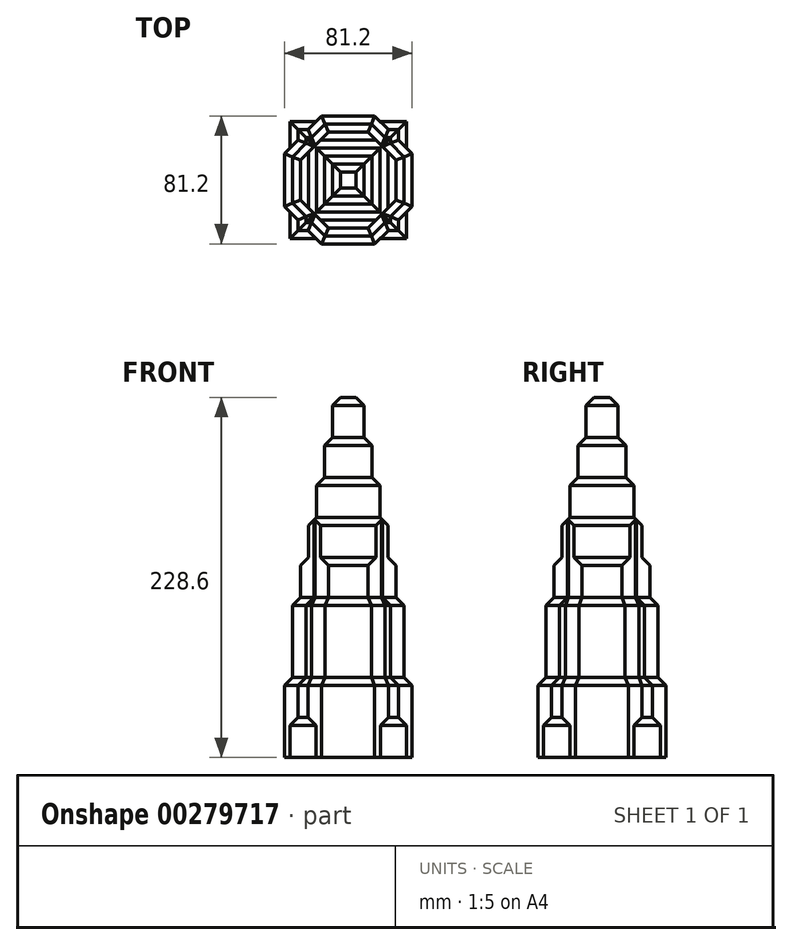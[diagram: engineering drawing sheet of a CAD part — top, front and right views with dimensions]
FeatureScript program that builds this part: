
annotation { "Feature Type Name" : "Feature", "Feature Type Description" : "" }
export const myFeature = defineFeature(function(context is Context, id is Id, definition is map)
    precondition{}
    {
        {
            var Q0;
            Q0=qCreatedBy(makeId("Top.planeOp"),FACE);
            var sketch = newSketch(context, id + "F0", { "sketchPlane" : qUnion([Q0])});
            skCircle(sketch, "E0.cCircle", {"center": v(0, 0) * mm, "radius": 37.05 * mm, "construction": true});
            skLineSegment(sketch, "E0.0", {"start": v(37.05, 37.05) * mm, "end": v(37.05, -37.05) * mm});
            skLineSegment(sketch, "E0.1", {"start": v(37.05, -37.05) * mm, "end": v(-37.05, -37.05) * mm});
            skLineSegment(sketch, "E0.2", {"start": v(-37.05, -37.05) * mm, "end": v(-37.05, 37.05) * mm});
            skLineSegment(sketch, "E0.3", {"start": v(-37.05, 37.05) * mm, "end": v(37.05, 37.05) * mm});
            skPoint(sketch, "E0.0.midPoint", {"position": v(37.05, 0) * mm});
            skCircle(sketch, "E1.cCircle", {"center": v(0, 0) * mm, "radius": 40.6 * mm, "construction": true});
            skLineSegment(sketch, "E1.0", {"start": v(40.6, 16.82) * mm, "end": v(40.6, -16.82) * mm});
            skLineSegment(sketch, "E1.1", {"start": v(40.6, -16.82) * mm, "end": v(16.82, -40.6) * mm});
            skLineSegment(sketch, "E1.2", {"start": v(16.82, -40.6) * mm, "end": v(-16.82, -40.6) * mm});
            skLineSegment(sketch, "E1.3", {"start": v(-16.82, -40.6) * mm, "end": v(-40.6, -16.82) * mm});
            skLineSegment(sketch, "E1.4", {"start": v(-40.6, -16.82) * mm, "end": v(-40.6, 16.82) * mm});
            skLineSegment(sketch, "E1.5", {"start": v(-40.6, 16.82) * mm, "end": v(-16.82, 40.6) * mm});
            skLineSegment(sketch, "E1.6", {"start": v(-16.82, 40.6) * mm, "end": v(16.82, 40.6) * mm});
            skLineSegment(sketch, "E1.7", {"start": v(16.82, 40.6) * mm, "end": v(40.6, 16.82) * mm});
            skPoint(sketch, "E1.0.midPoint", {"position": v(40.6, 0) * mm});
            skSolve(sketch);
        }
        {
            var Q0;
            Q0 = qSketchRegion(id + "F0", true);
            extrude(context, id + "F1", {"entities" : qUnion([Q0]), "depth" : 25.4 * mm});
        }
        {
            var Q0;
            {var subQ0=sQuery(id+"F0.wireOp",EDGE,"E0.3");Q0=makeQuery(id+"F1.opExtrude","CAP_EDGE",EDGE,{"disambiguationData":[OSD([subQ0]),TDD([makeQuery(id+"F0.imprint","IMPRINT",EDGE,{"disambiguationData":[TD([[makeQuery(id+"F0.imprint","INTERSECT",VERTEX,{"derivedFrom":[sQuery(id+"F0.wireOp",EDGE,"E0.2"),subQ0]}),-1.0]])],"derivedFrom":subQ0})])],"isStart":false});}
            var Q1;
            {var subQ0=sQuery(id+"F0.wireOp",EDGE,"E0.2");Q1=makeQuery(id+"F1.opExtrude","CAP_EDGE",EDGE,{"disambiguationData":[OSD([subQ0]),TDD([makeQuery(id+"F0.imprint","IMPRINT",EDGE,{"disambiguationData":[TD([[makeQuery(id+"F0.imprint","INTERSECT",VERTEX,{"derivedFrom":[subQ0,sQuery(id+"F0.wireOp",EDGE,"E0.3")]}),1.0]])],"derivedFrom":subQ0})])],"isStart":false});}
            var Q2;
            {var subQ0=sQuery(id+"F0.wireOp",EDGE,"E0.3");Q2=makeQuery(id+"F1.opExtrude","CAP_EDGE",EDGE,{"disambiguationData":[OSD([subQ0]),TDD([makeQuery(id+"F0.imprint","IMPRINT",EDGE,{"disambiguationData":[TD([[makeQuery(id+"F0.imprint","INTERSECT",VERTEX,{"derivedFrom":[sQuery(id+"F0.wireOp",EDGE,"E0.0"),subQ0]}),1.0]])],"derivedFrom":subQ0})])],"isStart":false});}
            var Q3;
            {var subQ0=sQuery(id+"F0.wireOp",EDGE,"E0.0");Q3=makeQuery(id+"F1.opExtrude","CAP_EDGE",EDGE,{"disambiguationData":[OSD([subQ0]),TDD([makeQuery(id+"F0.imprint","IMPRINT",EDGE,{"disambiguationData":[TD([[makeQuery(id+"F0.imprint","INTERSECT",VERTEX,{"derivedFrom":[subQ0,sQuery(id+"F0.wireOp",EDGE,"E0.3")]}),-1.0]])],"derivedFrom":subQ0})])],"isStart":false});}
            var Q4;
            {var subQ0=sQuery(id+"F0.wireOp",EDGE,"E0.0");Q4=makeQuery(id+"F1.opExtrude","CAP_EDGE",EDGE,{"disambiguationData":[OSD([subQ0]),TDD([makeQuery(id+"F0.imprint","IMPRINT",EDGE,{"disambiguationData":[TD([[makeQuery(id+"F0.imprint","INTERSECT",VERTEX,{"derivedFrom":[subQ0,sQuery(id+"F0.wireOp",EDGE,"E0.1")]}),1.0]])],"derivedFrom":subQ0})])],"isStart":false});}
            var Q5;
            {var subQ0=sQuery(id+"F0.wireOp",EDGE,"E0.1");Q5=makeQuery(id+"F1.opExtrude","CAP_EDGE",EDGE,{"disambiguationData":[OSD([subQ0]),TDD([makeQuery(id+"F0.imprint","IMPRINT",EDGE,{"disambiguationData":[TD([[makeQuery(id+"F0.imprint","INTERSECT",VERTEX,{"derivedFrom":[sQuery(id+"F0.wireOp",EDGE,"E0.0"),subQ0]}),-1.0]])],"derivedFrom":subQ0})])],"isStart":false});}
            var Q6;
            {var subQ0=sQuery(id+"F0.wireOp",EDGE,"E0.1");Q6=makeQuery(id+"F1.opExtrude","CAP_EDGE",EDGE,{"disambiguationData":[OSD([subQ0]),TDD([makeQuery(id+"F0.imprint","IMPRINT",EDGE,{"disambiguationData":[TD([[makeQuery(id+"F0.imprint","INTERSECT",VERTEX,{"derivedFrom":[subQ0,sQuery(id+"F0.wireOp",EDGE,"E0.2")]}),1.0]])],"derivedFrom":subQ0})])],"isStart":false});}
            var Q7;
            {var subQ0=sQuery(id+"F0.wireOp",EDGE,"E0.2");Q7=makeQuery(id+"F1.opExtrude","CAP_EDGE",EDGE,{"disambiguationData":[OSD([subQ0]),TDD([makeQuery(id+"F0.imprint","IMPRINT",EDGE,{"disambiguationData":[TD([[makeQuery(id+"F0.imprint","INTERSECT",VERTEX,{"derivedFrom":[sQuery(id+"F0.wireOp",EDGE,"E0.1"),subQ0]}),-1.0]])],"derivedFrom":subQ0})])],"isStart":false});}
            chamfer(context, id + "F2", {"entities" : qUnion([Q0, Q1, Q2, Q3, Q4, Q5, Q6, Q7]), "width" : 5.08 * mm, "tangentPropagation" : true});
        }
        {
            var Q0;
            Q0=makeQuery(id+"F1.opExtrude","CAP_FACE",FACE,{"disambiguationData":[OSD([sQuery(id+"F0.wireOp",EDGE,"E0.0"),sQuery(id+"F0.wireOp",EDGE,"E0.1"),sQuery(id+"F0.wireOp",EDGE,"E0.2"),sQuery(id+"F0.wireOp",EDGE,"E0.3"),sQuery(id+"F0.wireOp",EDGE,"E1.0"),sQuery(id+"F0.wireOp",EDGE,"E1.1"),sQuery(id+"F0.wireOp",EDGE,"E1.2"),sQuery(id+"F0.wireOp",EDGE,"E1.3"),sQuery(id+"F0.wireOp",EDGE,"E1.4"),sQuery(id+"F0.wireOp",EDGE,"E1.5"),sQuery(id+"F0.wireOp",EDGE,"E1.6"),sQuery(id+"F0.wireOp",EDGE,"E1.7")])],"isStart":false});
            extrude(context, id + "F3", {"entities" : qUnion([Q0]), "operationType" : NewBodyOperationType.ADD, "depth" : 25.4 * mm});
        }
        {
            var Q0;
            Q0=makeQuery(id+"F3.opExtrude","CAP_FACE",FACE,{"disambiguationData":[OSD([sQuery(id+"F0.wireOp",EDGE,"E0.0"),sQuery(id+"F0.wireOp",EDGE,"E0.1"),sQuery(id+"F0.wireOp",EDGE,"E0.2"),sQuery(id+"F0.wireOp",EDGE,"E0.3"),sQuery(id+"F0.wireOp",EDGE,"E1.0"),sQuery(id+"F0.wireOp",EDGE,"E1.1"),sQuery(id+"F0.wireOp",EDGE,"E1.2"),sQuery(id+"F0.wireOp",EDGE,"E1.3"),sQuery(id+"F0.wireOp",EDGE,"E1.4"),sQuery(id+"F0.wireOp",EDGE,"E1.5"),sQuery(id+"F0.wireOp",EDGE,"E1.6"),sQuery(id+"F0.wireOp",EDGE,"E1.7")])],"isStart":false});
            chamfer(context, id + "F4", {"entities" : qUnion([Q0]), "width" : 5.08 * mm, "tangentPropagation" : true});
        }
        {
            var Q0;
            Q0=makeQuery(id+"F3.opExtrude","CAP_FACE",FACE,{"disambiguationData":[OSD([sQuery(id+"F0.wireOp",EDGE,"E0.0"),sQuery(id+"F0.wireOp",EDGE,"E0.1"),sQuery(id+"F0.wireOp",EDGE,"E0.2"),sQuery(id+"F0.wireOp",EDGE,"E0.3"),sQuery(id+"F0.wireOp",EDGE,"E1.0"),sQuery(id+"F0.wireOp",EDGE,"E1.1"),sQuery(id+"F0.wireOp",EDGE,"E1.2"),sQuery(id+"F0.wireOp",EDGE,"E1.3"),sQuery(id+"F0.wireOp",EDGE,"E1.4"),sQuery(id+"F0.wireOp",EDGE,"E1.5"),sQuery(id+"F0.wireOp",EDGE,"E1.6"),sQuery(id+"F0.wireOp",EDGE,"E1.7")])],"isStart":false});
            extrude(context, id + "F5", {"entities" : qUnion([Q0]), "operationType" : NewBodyOperationType.ADD, "depth" : 25.4 * mm});
        }
        {
            var Q0;
            Q0=makeQuery(id+"F5.opExtrude","CAP_FACE",FACE,{"disambiguationData":[OSD([sQuery(id+"F0.wireOp",EDGE,"E0.0"),sQuery(id+"F0.wireOp",EDGE,"E0.1"),sQuery(id+"F0.wireOp",EDGE,"E0.2"),sQuery(id+"F0.wireOp",EDGE,"E0.3"),sQuery(id+"F0.wireOp",EDGE,"E1.0"),sQuery(id+"F0.wireOp",EDGE,"E1.1"),sQuery(id+"F0.wireOp",EDGE,"E1.2"),sQuery(id+"F0.wireOp",EDGE,"E1.3"),sQuery(id+"F0.wireOp",EDGE,"E1.4"),sQuery(id+"F0.wireOp",EDGE,"E1.5"),sQuery(id+"F0.wireOp",EDGE,"E1.6"),sQuery(id+"F0.wireOp",EDGE,"E1.7")])],"isStart":false});
            extrude(context, id + "F6", {"entities" : qUnion([Q0]), "operationType" : NewBodyOperationType.ADD, "depth" : 25.4 * mm});
        }
        {
            var Q0;
            Q0=makeQuery(id+"F6.opExtrude","CAP_FACE",FACE,{"disambiguationData":[OSD([sQuery(id+"F0.wireOp",EDGE,"E0.0"),sQuery(id+"F0.wireOp",EDGE,"E0.1"),sQuery(id+"F0.wireOp",EDGE,"E0.2"),sQuery(id+"F0.wireOp",EDGE,"E0.3"),sQuery(id+"F0.wireOp",EDGE,"E1.0"),sQuery(id+"F0.wireOp",EDGE,"E1.1"),sQuery(id+"F0.wireOp",EDGE,"E1.2"),sQuery(id+"F0.wireOp",EDGE,"E1.3"),sQuery(id+"F0.wireOp",EDGE,"E1.4"),sQuery(id+"F0.wireOp",EDGE,"E1.5"),sQuery(id+"F0.wireOp",EDGE,"E1.6"),sQuery(id+"F0.wireOp",EDGE,"E1.7")])],"isStart":false});
            chamfer(context, id + "F7", {"entities" : qUnion([Q0]), "width" : 5.08 * mm, "tangentPropagation" : true});
        }
        {
            var Q0;
            Q0=makeQuery(id+"F6.opExtrude","CAP_FACE",FACE,{"disambiguationData":[OSD([sQuery(id+"F0.wireOp",EDGE,"E0.0"),sQuery(id+"F0.wireOp",EDGE,"E0.1"),sQuery(id+"F0.wireOp",EDGE,"E0.2"),sQuery(id+"F0.wireOp",EDGE,"E0.3"),sQuery(id+"F0.wireOp",EDGE,"E1.0"),sQuery(id+"F0.wireOp",EDGE,"E1.1"),sQuery(id+"F0.wireOp",EDGE,"E1.2"),sQuery(id+"F0.wireOp",EDGE,"E1.3"),sQuery(id+"F0.wireOp",EDGE,"E1.4"),sQuery(id+"F0.wireOp",EDGE,"E1.5"),sQuery(id+"F0.wireOp",EDGE,"E1.6"),sQuery(id+"F0.wireOp",EDGE,"E1.7")])],"isStart":false});
            extrude(context, id + "F8", {"entities" : qUnion([Q0]), "operationType" : NewBodyOperationType.ADD, "depth" : 25.4 * mm});
        }
        {
            var Q0;
            {var subQ0=sQuery(id+"F0.wireOp",EDGE,"E1.7");var subQ1=sQuery(id+"F0.wireOp",EDGE,"E1.6");var subQ2=sQuery(id+"F0.wireOp",EDGE,"E1.5");var subQ3=sQuery(id+"F0.wireOp",EDGE,"E1.4");var subQ4=sQuery(id+"F0.wireOp",EDGE,"E1.3");var subQ5=sQuery(id+"F0.wireOp",EDGE,"E1.2");var subQ6=sQuery(id+"F0.wireOp",EDGE,"E1.1");var subQ7=sQuery(id+"F0.wireOp",EDGE,"E1.0");var subQ8=sQuery(id+"F0.wireOp",EDGE,"E0.3");var subQ9=sQuery(id+"F0.wireOp",EDGE,"E0.2");var subQ10=sQuery(id+"F0.wireOp",EDGE,"E0.1");var subQ11=sQuery(id+"F0.wireOp",EDGE,"E0.0");Q0=makeQuery(id+"F8.opExtrude","CAP_EDGE",EDGE,{"disambiguationData":[OSD([subQ11,subQ10,subQ9,subQ8,subQ7,subQ6,subQ5,subQ4,subQ3,subQ2,subQ1,subQ0]),TDD([makeQuery(id+"F7.opChamfer","BLEND_EDGE",EDGE,{"blendedFrom":[makeQuery(id+"F6.opExtrude","CAP_EDGE",EDGE,{"disambiguationData":[OSD([subQ11,subQ10,subQ9,subQ8,subQ7,subQ6,subQ5,subQ4,subQ3,subQ2,subQ1,subQ0]),TDD([makeQuery(id+"F5.opExtrude","CAP_EDGE",EDGE,{"disambiguationData":[OSD([subQ11,subQ10,subQ9,subQ8,subQ7,subQ6,subQ5,subQ4,subQ3,subQ2,subQ1,subQ0]),TDD([makeQuery(id+"F4.opChamfer","BLEND_EDGE",EDGE,{"blendedFrom":[makeQuery(id+"F3.opExtrude","CAP_EDGE",EDGE,{"disambiguationData":[OSD([subQ1])],"isStart":false}),makeQuery(id+"F3.opExtrude","CAP_FACE",FACE,{"disambiguationData":[OSD([subQ11,subQ10,subQ9,subQ8,subQ7,subQ6,subQ5,subQ4,subQ3,subQ2,subQ1,subQ0])],"isStart":false})],"blendedInto":[makeQuery(id+"F3.opExtrude","CAP_FACE",FACE,{"disambiguationData":[OSD([subQ11,subQ10,subQ9,subQ8,subQ7,subQ6,subQ5,subQ4,subQ3,subQ2,subQ1,subQ0])],"isStart":false})]})])],"isStart":false})])],"isStart":false}),makeQuery(id+"F6.opExtrude","CAP_FACE",FACE,{"disambiguationData":[OSD([subQ11,subQ10,subQ9,subQ8,subQ7,subQ6,subQ5,subQ4,subQ3,subQ2,subQ1,subQ0])],"isStart":false})],"blendedInto":[makeQuery(id+"F6.opExtrude","CAP_FACE",FACE,{"disambiguationData":[OSD([subQ11,subQ10,subQ9,subQ8,subQ7,subQ6,subQ5,subQ4,subQ3,subQ2,subQ1,subQ0])],"isStart":false})]})])],"isStart":false});}
            var Q1;
            {var subQ0=sQuery(id+"F0.wireOp",EDGE,"E1.7");var subQ1=sQuery(id+"F0.wireOp",EDGE,"E1.6");var subQ2=sQuery(id+"F0.wireOp",EDGE,"E1.5");var subQ3=sQuery(id+"F0.wireOp",EDGE,"E1.4");var subQ4=sQuery(id+"F0.wireOp",EDGE,"E1.3");var subQ5=sQuery(id+"F0.wireOp",EDGE,"E1.2");var subQ6=sQuery(id+"F0.wireOp",EDGE,"E1.1");var subQ7=sQuery(id+"F0.wireOp",EDGE,"E1.0");var subQ8=sQuery(id+"F0.wireOp",EDGE,"E0.3");var subQ9=sQuery(id+"F0.wireOp",EDGE,"E0.2");var subQ10=sQuery(id+"F0.wireOp",EDGE,"E0.1");var subQ11=sQuery(id+"F0.wireOp",EDGE,"E0.0");Q1=makeQuery(id+"F8.opExtrude","CAP_EDGE",EDGE,{"disambiguationData":[OSD([subQ11,subQ10,subQ9,subQ8,subQ7,subQ6,subQ5,subQ4,subQ3,subQ2,subQ1,subQ0]),TDD([makeQuery(id+"F7.opChamfer","BLEND_EDGE",EDGE,{"blendedFrom":[makeQuery(id+"F6.opExtrude","CAP_EDGE",EDGE,{"disambiguationData":[OSD([subQ11,subQ10,subQ9,subQ8,subQ7,subQ6,subQ5,subQ4,subQ3,subQ2,subQ1,subQ0]),TDD([makeQuery(id+"F5.opExtrude","CAP_EDGE",EDGE,{"disambiguationData":[OSD([subQ11,subQ10,subQ9,subQ8,subQ7,subQ6,subQ5,subQ4,subQ3,subQ2,subQ1,subQ0]),TDD([makeQuery(id+"F4.opChamfer","BLEND_EDGE",EDGE,{"blendedFrom":[makeQuery(id+"F3.opExtrude","CAP_EDGE",EDGE,{"disambiguationData":[OSD([subQ3])],"isStart":false}),makeQuery(id+"F3.opExtrude","CAP_FACE",FACE,{"disambiguationData":[OSD([subQ11,subQ10,subQ9,subQ8,subQ7,subQ6,subQ5,subQ4,subQ3,subQ2,subQ1,subQ0])],"isStart":false})],"blendedInto":[makeQuery(id+"F3.opExtrude","CAP_FACE",FACE,{"disambiguationData":[OSD([subQ11,subQ10,subQ9,subQ8,subQ7,subQ6,subQ5,subQ4,subQ3,subQ2,subQ1,subQ0])],"isStart":false})]})])],"isStart":false})])],"isStart":false}),makeQuery(id+"F6.opExtrude","CAP_FACE",FACE,{"disambiguationData":[OSD([subQ11,subQ10,subQ9,subQ8,subQ7,subQ6,subQ5,subQ4,subQ3,subQ2,subQ1,subQ0])],"isStart":false})],"blendedInto":[makeQuery(id+"F6.opExtrude","CAP_FACE",FACE,{"disambiguationData":[OSD([subQ11,subQ10,subQ9,subQ8,subQ7,subQ6,subQ5,subQ4,subQ3,subQ2,subQ1,subQ0])],"isStart":false})]})])],"isStart":false});}
            var Q2;
            {var subQ0=sQuery(id+"F0.wireOp",EDGE,"E1.7");var subQ1=sQuery(id+"F0.wireOp",EDGE,"E1.6");var subQ2=sQuery(id+"F0.wireOp",EDGE,"E1.5");var subQ3=sQuery(id+"F0.wireOp",EDGE,"E1.4");var subQ4=sQuery(id+"F0.wireOp",EDGE,"E1.3");var subQ5=sQuery(id+"F0.wireOp",EDGE,"E1.2");var subQ6=sQuery(id+"F0.wireOp",EDGE,"E1.1");var subQ7=sQuery(id+"F0.wireOp",EDGE,"E1.0");var subQ8=sQuery(id+"F0.wireOp",EDGE,"E0.3");var subQ9=sQuery(id+"F0.wireOp",EDGE,"E0.2");var subQ10=sQuery(id+"F0.wireOp",EDGE,"E0.1");var subQ11=sQuery(id+"F0.wireOp",EDGE,"E0.0");Q2=makeQuery(id+"F8.opExtrude","CAP_EDGE",EDGE,{"disambiguationData":[OSD([subQ11,subQ10,subQ9,subQ8,subQ7,subQ6,subQ5,subQ4,subQ3,subQ2,subQ1,subQ0]),TDD([makeQuery(id+"F7.opChamfer","BLEND_EDGE",EDGE,{"blendedFrom":[makeQuery(id+"F6.opExtrude","CAP_EDGE",EDGE,{"disambiguationData":[OSD([subQ11,subQ10,subQ9,subQ8,subQ7,subQ6,subQ5,subQ4,subQ3,subQ2,subQ1,subQ0]),TDD([makeQuery(id+"F5.opExtrude","CAP_EDGE",EDGE,{"disambiguationData":[OSD([subQ11,subQ10,subQ9,subQ8,subQ7,subQ6,subQ5,subQ4,subQ3,subQ2,subQ1,subQ0]),TDD([makeQuery(id+"F4.opChamfer","BLEND_EDGE",EDGE,{"blendedFrom":[makeQuery(id+"F3.opExtrude","CAP_EDGE",EDGE,{"disambiguationData":[OSD([subQ5])],"isStart":false}),makeQuery(id+"F3.opExtrude","CAP_FACE",FACE,{"disambiguationData":[OSD([subQ11,subQ10,subQ9,subQ8,subQ7,subQ6,subQ5,subQ4,subQ3,subQ2,subQ1,subQ0])],"isStart":false})],"blendedInto":[makeQuery(id+"F3.opExtrude","CAP_FACE",FACE,{"disambiguationData":[OSD([subQ11,subQ10,subQ9,subQ8,subQ7,subQ6,subQ5,subQ4,subQ3,subQ2,subQ1,subQ0])],"isStart":false})]})])],"isStart":false})])],"isStart":false}),makeQuery(id+"F6.opExtrude","CAP_FACE",FACE,{"disambiguationData":[OSD([subQ11,subQ10,subQ9,subQ8,subQ7,subQ6,subQ5,subQ4,subQ3,subQ2,subQ1,subQ0])],"isStart":false})],"blendedInto":[makeQuery(id+"F6.opExtrude","CAP_FACE",FACE,{"disambiguationData":[OSD([subQ11,subQ10,subQ9,subQ8,subQ7,subQ6,subQ5,subQ4,subQ3,subQ2,subQ1,subQ0])],"isStart":false})]})])],"isStart":false});}
            var Q3;
            {var subQ0=sQuery(id+"F0.wireOp",EDGE,"E1.7");var subQ1=sQuery(id+"F0.wireOp",EDGE,"E1.6");var subQ2=sQuery(id+"F0.wireOp",EDGE,"E1.5");var subQ3=sQuery(id+"F0.wireOp",EDGE,"E1.4");var subQ4=sQuery(id+"F0.wireOp",EDGE,"E1.3");var subQ5=sQuery(id+"F0.wireOp",EDGE,"E1.2");var subQ6=sQuery(id+"F0.wireOp",EDGE,"E1.1");var subQ7=sQuery(id+"F0.wireOp",EDGE,"E1.0");var subQ8=sQuery(id+"F0.wireOp",EDGE,"E0.3");var subQ9=sQuery(id+"F0.wireOp",EDGE,"E0.2");var subQ10=sQuery(id+"F0.wireOp",EDGE,"E0.1");var subQ11=sQuery(id+"F0.wireOp",EDGE,"E0.0");Q3=makeQuery(id+"F8.opExtrude","CAP_EDGE",EDGE,{"disambiguationData":[OSD([subQ11,subQ10,subQ9,subQ8,subQ7,subQ6,subQ5,subQ4,subQ3,subQ2,subQ1,subQ0]),TDD([makeQuery(id+"F7.opChamfer","BLEND_EDGE",EDGE,{"blendedFrom":[makeQuery(id+"F6.opExtrude","CAP_EDGE",EDGE,{"disambiguationData":[OSD([subQ11,subQ10,subQ9,subQ8,subQ7,subQ6,subQ5,subQ4,subQ3,subQ2,subQ1,subQ0]),TDD([makeQuery(id+"F5.opExtrude","CAP_EDGE",EDGE,{"disambiguationData":[OSD([subQ11,subQ10,subQ9,subQ8,subQ7,subQ6,subQ5,subQ4,subQ3,subQ2,subQ1,subQ0]),TDD([makeQuery(id+"F4.opChamfer","BLEND_EDGE",EDGE,{"blendedFrom":[makeQuery(id+"F3.opExtrude","CAP_EDGE",EDGE,{"disambiguationData":[OSD([subQ7])],"isStart":false}),makeQuery(id+"F3.opExtrude","CAP_FACE",FACE,{"disambiguationData":[OSD([subQ11,subQ10,subQ9,subQ8,subQ7,subQ6,subQ5,subQ4,subQ3,subQ2,subQ1,subQ0])],"isStart":false})],"blendedInto":[makeQuery(id+"F3.opExtrude","CAP_FACE",FACE,{"disambiguationData":[OSD([subQ11,subQ10,subQ9,subQ8,subQ7,subQ6,subQ5,subQ4,subQ3,subQ2,subQ1,subQ0])],"isStart":false})]})])],"isStart":false})])],"isStart":false}),makeQuery(id+"F6.opExtrude","CAP_FACE",FACE,{"disambiguationData":[OSD([subQ11,subQ10,subQ9,subQ8,subQ7,subQ6,subQ5,subQ4,subQ3,subQ2,subQ1,subQ0])],"isStart":false})],"blendedInto":[makeQuery(id+"F6.opExtrude","CAP_FACE",FACE,{"disambiguationData":[OSD([subQ11,subQ10,subQ9,subQ8,subQ7,subQ6,subQ5,subQ4,subQ3,subQ2,subQ1,subQ0])],"isStart":false})]})])],"isStart":false});}
            chamfer(context, id + "F9", {"entities" : qUnion([Q0, Q1, Q2, Q3]), "width" : 5.08 * mm, "tangentPropagation" : true});
        }
        {
            var Q0;
            Q0=makeQuery(id+"F8.opExtrude","CAP_FACE",FACE,{"disambiguationData":[OSD([sQuery(id+"F0.wireOp",EDGE,"E0.0"),sQuery(id+"F0.wireOp",EDGE,"E0.1"),sQuery(id+"F0.wireOp",EDGE,"E0.2"),sQuery(id+"F0.wireOp",EDGE,"E0.3"),sQuery(id+"F0.wireOp",EDGE,"E1.0"),sQuery(id+"F0.wireOp",EDGE,"E1.1"),sQuery(id+"F0.wireOp",EDGE,"E1.2"),sQuery(id+"F0.wireOp",EDGE,"E1.3"),sQuery(id+"F0.wireOp",EDGE,"E1.4"),sQuery(id+"F0.wireOp",EDGE,"E1.5"),sQuery(id+"F0.wireOp",EDGE,"E1.6"),sQuery(id+"F0.wireOp",EDGE,"E1.7")])],"isStart":false});
            extrude(context, id + "F10", {"entities" : qUnion([Q0]), "operationType" : NewBodyOperationType.ADD, "depth" : 25.4 * mm});
        }
        {
            var Q0;
            {var subQ0=sQuery(id+"F0.wireOp",EDGE,"E1.7");var subQ1=sQuery(id+"F0.wireOp",EDGE,"E1.6");var subQ2=sQuery(id+"F0.wireOp",EDGE,"E1.5");var subQ3=sQuery(id+"F0.wireOp",EDGE,"E1.4");var subQ4=sQuery(id+"F0.wireOp",EDGE,"E1.3");var subQ5=sQuery(id+"F0.wireOp",EDGE,"E1.2");var subQ6=sQuery(id+"F0.wireOp",EDGE,"E1.1");var subQ7=sQuery(id+"F0.wireOp",EDGE,"E1.0");var subQ8=sQuery(id+"F0.wireOp",EDGE,"E0.3");var subQ9=sQuery(id+"F0.wireOp",EDGE,"E0.2");var subQ10=sQuery(id+"F0.wireOp",EDGE,"E0.1");var subQ11=sQuery(id+"F0.wireOp",EDGE,"E0.0");Q0=makeQuery(id+"F10.opExtrude","CAP_EDGE",EDGE,{"disambiguationData":[OSD([subQ11,subQ10,subQ9,subQ8,subQ7,subQ6,subQ5,subQ4,subQ3,subQ2,subQ1,subQ0]),TDD([makeQuery(id+"F9.opChamfer","BLEND_EDGE",EDGE,{"blendedFrom":[makeQuery(id+"F8.opExtrude","CAP_EDGE",EDGE,{"disambiguationData":[OSD([subQ11,subQ10,subQ9,subQ8,subQ7,subQ6,subQ5,subQ4,subQ3,subQ2,subQ1,subQ0]),TDD([makeQuery(id+"F7.opChamfer","BLEND_EDGE",EDGE,{"blendedFrom":[makeQuery(id+"F6.opExtrude","CAP_EDGE",EDGE,{"disambiguationData":[OSD([subQ11,subQ10,subQ9,subQ8,subQ7,subQ6,subQ5,subQ4,subQ3,subQ2,subQ1,subQ0]),TDD([makeQuery(id+"F5.opExtrude","CAP_EDGE",EDGE,{"disambiguationData":[OSD([subQ11,subQ10,subQ9,subQ8,subQ7,subQ6,subQ5,subQ4,subQ3,subQ2,subQ1,subQ0]),TDD([makeQuery(id+"F4.opChamfer","BLEND_EDGE",EDGE,{"blendedFrom":[makeQuery(id+"F3.opExtrude","CAP_EDGE",EDGE,{"disambiguationData":[OSD([subQ1])],"isStart":false}),makeQuery(id+"F3.opExtrude","CAP_FACE",FACE,{"disambiguationData":[OSD([subQ11,subQ10,subQ9,subQ8,subQ7,subQ6,subQ5,subQ4,subQ3,subQ2,subQ1,subQ0])],"isStart":false})],"blendedInto":[makeQuery(id+"F3.opExtrude","CAP_FACE",FACE,{"disambiguationData":[OSD([subQ11,subQ10,subQ9,subQ8,subQ7,subQ6,subQ5,subQ4,subQ3,subQ2,subQ1,subQ0])],"isStart":false})]})])],"isStart":false})])],"isStart":false}),makeQuery(id+"F6.opExtrude","CAP_FACE",FACE,{"disambiguationData":[OSD([subQ11,subQ10,subQ9,subQ8,subQ7,subQ6,subQ5,subQ4,subQ3,subQ2,subQ1,subQ0])],"isStart":false})],"blendedInto":[makeQuery(id+"F6.opExtrude","CAP_FACE",FACE,{"disambiguationData":[OSD([subQ11,subQ10,subQ9,subQ8,subQ7,subQ6,subQ5,subQ4,subQ3,subQ2,subQ1,subQ0])],"isStart":false})]})])],"isStart":false}),makeQuery(id+"F8.opExtrude","CAP_FACE",FACE,{"disambiguationData":[OSD([subQ11,subQ10,subQ9,subQ8,subQ7,subQ6,subQ5,subQ4,subQ3,subQ2,subQ1,subQ0])],"isStart":false})],"blendedInto":[makeQuery(id+"F8.opExtrude","CAP_FACE",FACE,{"disambiguationData":[OSD([subQ11,subQ10,subQ9,subQ8,subQ7,subQ6,subQ5,subQ4,subQ3,subQ2,subQ1,subQ0])],"isStart":false})]})])],"isStart":false});}
            var Q1;
            {var subQ0=sQuery(id+"F0.wireOp",EDGE,"E1.7");var subQ1=sQuery(id+"F0.wireOp",EDGE,"E1.6");var subQ2=sQuery(id+"F0.wireOp",EDGE,"E1.5");var subQ3=sQuery(id+"F0.wireOp",EDGE,"E1.4");var subQ4=sQuery(id+"F0.wireOp",EDGE,"E1.3");var subQ5=sQuery(id+"F0.wireOp",EDGE,"E1.2");var subQ6=sQuery(id+"F0.wireOp",EDGE,"E1.1");var subQ7=sQuery(id+"F0.wireOp",EDGE,"E1.0");var subQ8=sQuery(id+"F0.wireOp",EDGE,"E0.3");var subQ9=sQuery(id+"F0.wireOp",EDGE,"E0.2");var subQ10=sQuery(id+"F0.wireOp",EDGE,"E0.1");var subQ11=sQuery(id+"F0.wireOp",EDGE,"E0.0");Q1=makeQuery(id+"F10.opExtrude","CAP_EDGE",EDGE,{"disambiguationData":[OSD([subQ11,subQ10,subQ9,subQ8,subQ7,subQ6,subQ5,subQ4,subQ3,subQ2,subQ1,subQ0]),TDD([makeQuery(id+"F9.opChamfer","BLEND_EDGE",EDGE,{"blendedFrom":[makeQuery(id+"F8.opExtrude","CAP_EDGE",EDGE,{"disambiguationData":[OSD([subQ11,subQ10,subQ9,subQ8,subQ7,subQ6,subQ5,subQ4,subQ3,subQ2,subQ1,subQ0]),TDD([makeQuery(id+"F7.opChamfer","BLEND_EDGE",EDGE,{"blendedFrom":[makeQuery(id+"F6.opExtrude","CAP_EDGE",EDGE,{"disambiguationData":[OSD([subQ11,subQ10,subQ9,subQ8,subQ7,subQ6,subQ5,subQ4,subQ3,subQ2,subQ1,subQ0]),TDD([makeQuery(id+"F5.opExtrude","CAP_EDGE",EDGE,{"disambiguationData":[OSD([subQ11,subQ10,subQ9,subQ8,subQ7,subQ6,subQ5,subQ4,subQ3,subQ2,subQ1,subQ0]),TDD([makeQuery(id+"F4.opChamfer","BLEND_EDGE",EDGE,{"blendedFrom":[makeQuery(id+"F3.opExtrude","CAP_EDGE",EDGE,{"disambiguationData":[OSD([subQ3])],"isStart":false}),makeQuery(id+"F3.opExtrude","CAP_FACE",FACE,{"disambiguationData":[OSD([subQ11,subQ10,subQ9,subQ8,subQ7,subQ6,subQ5,subQ4,subQ3,subQ2,subQ1,subQ0])],"isStart":false})],"blendedInto":[makeQuery(id+"F3.opExtrude","CAP_FACE",FACE,{"disambiguationData":[OSD([subQ11,subQ10,subQ9,subQ8,subQ7,subQ6,subQ5,subQ4,subQ3,subQ2,subQ1,subQ0])],"isStart":false})]})])],"isStart":false})])],"isStart":false}),makeQuery(id+"F6.opExtrude","CAP_FACE",FACE,{"disambiguationData":[OSD([subQ11,subQ10,subQ9,subQ8,subQ7,subQ6,subQ5,subQ4,subQ3,subQ2,subQ1,subQ0])],"isStart":false})],"blendedInto":[makeQuery(id+"F6.opExtrude","CAP_FACE",FACE,{"disambiguationData":[OSD([subQ11,subQ10,subQ9,subQ8,subQ7,subQ6,subQ5,subQ4,subQ3,subQ2,subQ1,subQ0])],"isStart":false})]})])],"isStart":false}),makeQuery(id+"F8.opExtrude","CAP_FACE",FACE,{"disambiguationData":[OSD([subQ11,subQ10,subQ9,subQ8,subQ7,subQ6,subQ5,subQ4,subQ3,subQ2,subQ1,subQ0])],"isStart":false})],"blendedInto":[makeQuery(id+"F8.opExtrude","CAP_FACE",FACE,{"disambiguationData":[OSD([subQ11,subQ10,subQ9,subQ8,subQ7,subQ6,subQ5,subQ4,subQ3,subQ2,subQ1,subQ0])],"isStart":false})]})])],"isStart":false});}
            var Q2;
            {var subQ0=sQuery(id+"F0.wireOp",EDGE,"E1.7");var subQ1=sQuery(id+"F0.wireOp",EDGE,"E1.6");var subQ2=sQuery(id+"F0.wireOp",EDGE,"E1.5");var subQ3=sQuery(id+"F0.wireOp",EDGE,"E1.4");var subQ4=sQuery(id+"F0.wireOp",EDGE,"E1.3");var subQ5=sQuery(id+"F0.wireOp",EDGE,"E1.2");var subQ6=sQuery(id+"F0.wireOp",EDGE,"E1.1");var subQ7=sQuery(id+"F0.wireOp",EDGE,"E1.0");var subQ8=sQuery(id+"F0.wireOp",EDGE,"E0.3");var subQ9=sQuery(id+"F0.wireOp",EDGE,"E0.2");var subQ10=sQuery(id+"F0.wireOp",EDGE,"E0.1");var subQ11=sQuery(id+"F0.wireOp",EDGE,"E0.0");Q2=makeQuery(id+"F10.opExtrude","CAP_EDGE",EDGE,{"disambiguationData":[OSD([subQ11,subQ10,subQ9,subQ8,subQ7,subQ6,subQ5,subQ4,subQ3,subQ2,subQ1,subQ0]),TDD([makeQuery(id+"F9.opChamfer","BLEND_EDGE",EDGE,{"blendedFrom":[makeQuery(id+"F8.opExtrude","CAP_EDGE",EDGE,{"disambiguationData":[OSD([subQ11,subQ10,subQ9,subQ8,subQ7,subQ6,subQ5,subQ4,subQ3,subQ2,subQ1,subQ0]),TDD([makeQuery(id+"F7.opChamfer","BLEND_EDGE",EDGE,{"blendedFrom":[makeQuery(id+"F6.opExtrude","CAP_EDGE",EDGE,{"disambiguationData":[OSD([subQ11,subQ10,subQ9,subQ8,subQ7,subQ6,subQ5,subQ4,subQ3,subQ2,subQ1,subQ0]),TDD([makeQuery(id+"F5.opExtrude","CAP_EDGE",EDGE,{"disambiguationData":[OSD([subQ11,subQ10,subQ9,subQ8,subQ7,subQ6,subQ5,subQ4,subQ3,subQ2,subQ1,subQ0]),TDD([makeQuery(id+"F4.opChamfer","BLEND_EDGE",EDGE,{"blendedFrom":[makeQuery(id+"F3.opExtrude","CAP_EDGE",EDGE,{"disambiguationData":[OSD([subQ5])],"isStart":false}),makeQuery(id+"F3.opExtrude","CAP_FACE",FACE,{"disambiguationData":[OSD([subQ11,subQ10,subQ9,subQ8,subQ7,subQ6,subQ5,subQ4,subQ3,subQ2,subQ1,subQ0])],"isStart":false})],"blendedInto":[makeQuery(id+"F3.opExtrude","CAP_FACE",FACE,{"disambiguationData":[OSD([subQ11,subQ10,subQ9,subQ8,subQ7,subQ6,subQ5,subQ4,subQ3,subQ2,subQ1,subQ0])],"isStart":false})]})])],"isStart":false})])],"isStart":false}),makeQuery(id+"F6.opExtrude","CAP_FACE",FACE,{"disambiguationData":[OSD([subQ11,subQ10,subQ9,subQ8,subQ7,subQ6,subQ5,subQ4,subQ3,subQ2,subQ1,subQ0])],"isStart":false})],"blendedInto":[makeQuery(id+"F6.opExtrude","CAP_FACE",FACE,{"disambiguationData":[OSD([subQ11,subQ10,subQ9,subQ8,subQ7,subQ6,subQ5,subQ4,subQ3,subQ2,subQ1,subQ0])],"isStart":false})]})])],"isStart":false}),makeQuery(id+"F8.opExtrude","CAP_FACE",FACE,{"disambiguationData":[OSD([subQ11,subQ10,subQ9,subQ8,subQ7,subQ6,subQ5,subQ4,subQ3,subQ2,subQ1,subQ0])],"isStart":false})],"blendedInto":[makeQuery(id+"F8.opExtrude","CAP_FACE",FACE,{"disambiguationData":[OSD([subQ11,subQ10,subQ9,subQ8,subQ7,subQ6,subQ5,subQ4,subQ3,subQ2,subQ1,subQ0])],"isStart":false})]})])],"isStart":false});}
            var Q3;
            {var subQ0=sQuery(id+"F0.wireOp",EDGE,"E1.7");var subQ1=sQuery(id+"F0.wireOp",EDGE,"E1.6");var subQ2=sQuery(id+"F0.wireOp",EDGE,"E1.5");var subQ3=sQuery(id+"F0.wireOp",EDGE,"E1.4");var subQ4=sQuery(id+"F0.wireOp",EDGE,"E1.3");var subQ5=sQuery(id+"F0.wireOp",EDGE,"E1.2");var subQ6=sQuery(id+"F0.wireOp",EDGE,"E1.1");var subQ7=sQuery(id+"F0.wireOp",EDGE,"E1.0");var subQ8=sQuery(id+"F0.wireOp",EDGE,"E0.3");var subQ9=sQuery(id+"F0.wireOp",EDGE,"E0.2");var subQ10=sQuery(id+"F0.wireOp",EDGE,"E0.1");var subQ11=sQuery(id+"F0.wireOp",EDGE,"E0.0");Q3=makeQuery(id+"F10.opExtrude","CAP_EDGE",EDGE,{"disambiguationData":[OSD([subQ11,subQ10,subQ9,subQ8,subQ7,subQ6,subQ5,subQ4,subQ3,subQ2,subQ1,subQ0]),TDD([makeQuery(id+"F9.opChamfer","BLEND_EDGE",EDGE,{"blendedFrom":[makeQuery(id+"F8.opExtrude","CAP_EDGE",EDGE,{"disambiguationData":[OSD([subQ11,subQ10,subQ9,subQ8,subQ7,subQ6,subQ5,subQ4,subQ3,subQ2,subQ1,subQ0]),TDD([makeQuery(id+"F7.opChamfer","BLEND_EDGE",EDGE,{"blendedFrom":[makeQuery(id+"F6.opExtrude","CAP_EDGE",EDGE,{"disambiguationData":[OSD([subQ11,subQ10,subQ9,subQ8,subQ7,subQ6,subQ5,subQ4,subQ3,subQ2,subQ1,subQ0]),TDD([makeQuery(id+"F5.opExtrude","CAP_EDGE",EDGE,{"disambiguationData":[OSD([subQ11,subQ10,subQ9,subQ8,subQ7,subQ6,subQ5,subQ4,subQ3,subQ2,subQ1,subQ0]),TDD([makeQuery(id+"F4.opChamfer","BLEND_EDGE",EDGE,{"blendedFrom":[makeQuery(id+"F3.opExtrude","CAP_EDGE",EDGE,{"disambiguationData":[OSD([subQ7])],"isStart":false}),makeQuery(id+"F3.opExtrude","CAP_FACE",FACE,{"disambiguationData":[OSD([subQ11,subQ10,subQ9,subQ8,subQ7,subQ6,subQ5,subQ4,subQ3,subQ2,subQ1,subQ0])],"isStart":false})],"blendedInto":[makeQuery(id+"F3.opExtrude","CAP_FACE",FACE,{"disambiguationData":[OSD([subQ11,subQ10,subQ9,subQ8,subQ7,subQ6,subQ5,subQ4,subQ3,subQ2,subQ1,subQ0])],"isStart":false})]})])],"isStart":false})])],"isStart":false}),makeQuery(id+"F6.opExtrude","CAP_FACE",FACE,{"disambiguationData":[OSD([subQ11,subQ10,subQ9,subQ8,subQ7,subQ6,subQ5,subQ4,subQ3,subQ2,subQ1,subQ0])],"isStart":false})],"blendedInto":[makeQuery(id+"F6.opExtrude","CAP_FACE",FACE,{"disambiguationData":[OSD([subQ11,subQ10,subQ9,subQ8,subQ7,subQ6,subQ5,subQ4,subQ3,subQ2,subQ1,subQ0])],"isStart":false})]})])],"isStart":false}),makeQuery(id+"F8.opExtrude","CAP_FACE",FACE,{"disambiguationData":[OSD([subQ11,subQ10,subQ9,subQ8,subQ7,subQ6,subQ5,subQ4,subQ3,subQ2,subQ1,subQ0])],"isStart":false})],"blendedInto":[makeQuery(id+"F8.opExtrude","CAP_FACE",FACE,{"disambiguationData":[OSD([subQ11,subQ10,subQ9,subQ8,subQ7,subQ6,subQ5,subQ4,subQ3,subQ2,subQ1,subQ0])],"isStart":false})]})])],"isStart":false});}
            chamfer(context, id + "F11", {"entities" : qUnion([Q0, Q1, Q2, Q3]), "width" : 5.08 * mm, "tangentPropagation" : true});
        }
        {
            var Q0;
            Q0=makeQuery(id+"F10.opExtrude","CAP_FACE",FACE,{"disambiguationData":[OSD([sQuery(id+"F0.wireOp",EDGE,"E0.0"),sQuery(id+"F0.wireOp",EDGE,"E0.1"),sQuery(id+"F0.wireOp",EDGE,"E0.2"),sQuery(id+"F0.wireOp",EDGE,"E0.3"),sQuery(id+"F0.wireOp",EDGE,"E1.0"),sQuery(id+"F0.wireOp",EDGE,"E1.1"),sQuery(id+"F0.wireOp",EDGE,"E1.2"),sQuery(id+"F0.wireOp",EDGE,"E1.3"),sQuery(id+"F0.wireOp",EDGE,"E1.4"),sQuery(id+"F0.wireOp",EDGE,"E1.5"),sQuery(id+"F0.wireOp",EDGE,"E1.6"),sQuery(id+"F0.wireOp",EDGE,"E1.7")])],"isStart":false});
            extrude(context, id + "F12", {"entities" : qUnion([Q0]), "operationType" : NewBodyOperationType.ADD, "depth" : 25.4 * mm});
        }
        {
            var Q0;
            Q0=makeQuery(id+"F12.opExtrude","CAP_FACE",FACE,{"disambiguationData":[OSD([sQuery(id+"F0.wireOp",EDGE,"E0.0"),sQuery(id+"F0.wireOp",EDGE,"E0.1"),sQuery(id+"F0.wireOp",EDGE,"E0.2"),sQuery(id+"F0.wireOp",EDGE,"E0.3"),sQuery(id+"F0.wireOp",EDGE,"E1.0"),sQuery(id+"F0.wireOp",EDGE,"E1.1"),sQuery(id+"F0.wireOp",EDGE,"E1.2"),sQuery(id+"F0.wireOp",EDGE,"E1.3"),sQuery(id+"F0.wireOp",EDGE,"E1.4"),sQuery(id+"F0.wireOp",EDGE,"E1.5"),sQuery(id+"F0.wireOp",EDGE,"E1.6"),sQuery(id+"F0.wireOp",EDGE,"E1.7")])],"isStart":false});
            chamfer(context, id + "F13", {"entities" : qUnion([Q0]), "width" : 5.08 * mm, "tangentPropagation" : true});
        }
        {
            var Q0;
            Q0=makeQuery(id+"F12.opExtrude","CAP_FACE",FACE,{"disambiguationData":[OSD([sQuery(id+"F0.wireOp",EDGE,"E0.0"),sQuery(id+"F0.wireOp",EDGE,"E0.1"),sQuery(id+"F0.wireOp",EDGE,"E0.2"),sQuery(id+"F0.wireOp",EDGE,"E0.3"),sQuery(id+"F0.wireOp",EDGE,"E1.0"),sQuery(id+"F0.wireOp",EDGE,"E1.1"),sQuery(id+"F0.wireOp",EDGE,"E1.2"),sQuery(id+"F0.wireOp",EDGE,"E1.3"),sQuery(id+"F0.wireOp",EDGE,"E1.4"),sQuery(id+"F0.wireOp",EDGE,"E1.5"),sQuery(id+"F0.wireOp",EDGE,"E1.6"),sQuery(id+"F0.wireOp",EDGE,"E1.7")])],"isStart":false});
            extrude(context, id + "F14", {"entities" : qUnion([Q0]), "operationType" : NewBodyOperationType.ADD, "depth" : 25.4 * mm});
        }
        {
            var Q0;
            Q0=makeQuery(id+"F14.opExtrude","CAP_FACE",FACE,{"disambiguationData":[OSD([sQuery(id+"F0.wireOp",EDGE,"E0.0"),sQuery(id+"F0.wireOp",EDGE,"E0.1"),sQuery(id+"F0.wireOp",EDGE,"E0.2"),sQuery(id+"F0.wireOp",EDGE,"E0.3"),sQuery(id+"F0.wireOp",EDGE,"E1.0"),sQuery(id+"F0.wireOp",EDGE,"E1.1"),sQuery(id+"F0.wireOp",EDGE,"E1.2"),sQuery(id+"F0.wireOp",EDGE,"E1.3"),sQuery(id+"F0.wireOp",EDGE,"E1.4"),sQuery(id+"F0.wireOp",EDGE,"E1.5"),sQuery(id+"F0.wireOp",EDGE,"E1.6"),sQuery(id+"F0.wireOp",EDGE,"E1.7")])],"isStart":false});
            chamfer(context, id + "F15", {"entities" : qUnion([Q0]), "width" : 5.08 * mm, "tangentPropagation" : true});
        }
        {
            var Q0;
            Q0=makeQuery(id+"F14.opExtrude","CAP_FACE",FACE,{"disambiguationData":[OSD([sQuery(id+"F0.wireOp",EDGE,"E0.0"),sQuery(id+"F0.wireOp",EDGE,"E0.1"),sQuery(id+"F0.wireOp",EDGE,"E0.2"),sQuery(id+"F0.wireOp",EDGE,"E0.3"),sQuery(id+"F0.wireOp",EDGE,"E1.0"),sQuery(id+"F0.wireOp",EDGE,"E1.1"),sQuery(id+"F0.wireOp",EDGE,"E1.2"),sQuery(id+"F0.wireOp",EDGE,"E1.3"),sQuery(id+"F0.wireOp",EDGE,"E1.4"),sQuery(id+"F0.wireOp",EDGE,"E1.5"),sQuery(id+"F0.wireOp",EDGE,"E1.6"),sQuery(id+"F0.wireOp",EDGE,"E1.7")])],"isStart":false});
            extrude(context, id + "F16", {"entities" : qUnion([Q0]), "operationType" : NewBodyOperationType.ADD, "depth" : 25.4 * mm});
        }
        {
            var Q0;
            Q0=makeQuery(id+"F16.opExtrude","CAP_FACE",FACE,{"disambiguationData":[OSD([sQuery(id+"F0.wireOp",EDGE,"E0.0"),sQuery(id+"F0.wireOp",EDGE,"E0.1"),sQuery(id+"F0.wireOp",EDGE,"E0.2"),sQuery(id+"F0.wireOp",EDGE,"E0.3"),sQuery(id+"F0.wireOp",EDGE,"E1.0"),sQuery(id+"F0.wireOp",EDGE,"E1.1"),sQuery(id+"F0.wireOp",EDGE,"E1.2"),sQuery(id+"F0.wireOp",EDGE,"E1.3"),sQuery(id+"F0.wireOp",EDGE,"E1.4"),sQuery(id+"F0.wireOp",EDGE,"E1.5"),sQuery(id+"F0.wireOp",EDGE,"E1.6"),sQuery(id+"F0.wireOp",EDGE,"E1.7")])],"isStart":false});
            chamfer(context, id + "F17", {"entities" : qUnion([Q0]), "width" : 5.08 * mm, "tangentPropagation" : true});
        }
    });
